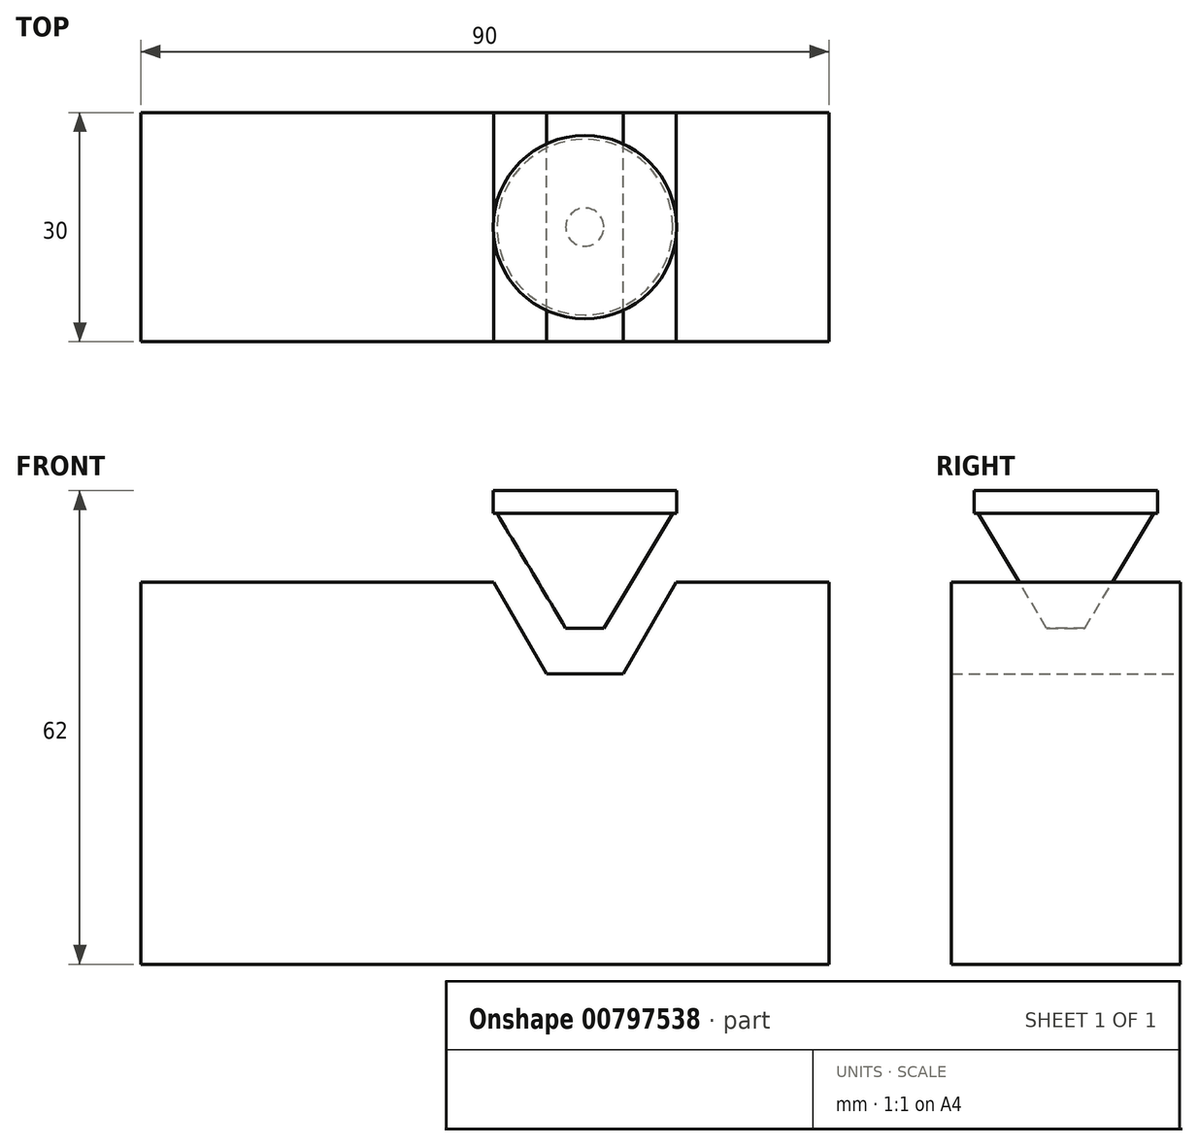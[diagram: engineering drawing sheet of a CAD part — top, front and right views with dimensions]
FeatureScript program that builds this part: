
annotation { "Feature Type Name" : "Feature", "Feature Type Description" : "" }
export const myFeature = defineFeature(function(context is Context, id is Id, definition is map)
    precondition{}
    {
        {
            var Q0;
            Q0=qCreatedBy(makeId("Front.planeOp"),FACE);
            var sketch = newSketch(context, id + "F0", { "sketchPlane" : qUnion([Q0])});
            skLineSegment(sketch, "E0", {"start": v(-90, 50) * mm, "end": v(-43.86, 50) * mm});
            skLineSegment(sketch, "E1", {"start": v(-43.86, 50) * mm, "end": v(-36.93, 38) * mm});
            skLineSegment(sketch, "E2", {"start": v(-36.93, 38) * mm, "end": v(-26.93, 38) * mm});
            skLineSegment(sketch, "E3", {"start": v(-26.93, 38) * mm, "end": v(-20, 50) * mm});
            skLineSegment(sketch, "E4", {"start": v(-20, 50) * mm, "end": v(0, 50) * mm});
            skLineSegment(sketch, "E5", {"start": v(0, 50) * mm, "end": v(0, 0) * mm});
            skLineSegment(sketch, "E6", {"start": v(0, 0) * mm, "end": v(-90, 0) * mm});
            skLineSegment(sketch, "E7", {"start": v(-90, 0) * mm, "end": v(-90, 50) * mm});
            skPoint(sketch, "E8", {"position": v(-31.93, 38) * mm});
            skLineSegment(sketch, "E9.bottom", {"start": v(-31.93, 38) * mm, "end": v(-29.43, 38) * mm});
            skLineSegment(sketch, "E9.top", {"start": v(-31.93, 44) * mm, "end": v(-29.43, 44) * mm});
            skLineSegment(sketch, "E9.left", {"start": v(-31.93, 38) * mm, "end": v(-31.93, 44) * mm});
            skLineSegment(sketch, "E9.right", {"start": v(-29.43, 38) * mm, "end": v(-29.43, 44) * mm});
            skLineSegment(sketch, "E10", {"start": v(-29.43, 44) * mm, "end": v(-20.43, 59) * mm});
            skLineSegment(sketch, "E11", {"start": v(-20.43, 59) * mm, "end": v(-31.93, 59) * mm});
            skLineSegment(sketch, "E12", {"start": v(-31.93, 59) * mm, "end": v(-31.93, 44) * mm});
            skLineSegment(sketch, "E13.bottom", {"start": v(-31.93, 59) * mm, "end": v(-19.93, 59) * mm});
            skLineSegment(sketch, "E13.top", {"start": v(-31.93, 62) * mm, "end": v(-19.93, 62) * mm});
            skLineSegment(sketch, "E13.left", {"start": v(-31.93, 59) * mm, "end": v(-31.93, 62) * mm});
            skLineSegment(sketch, "E13.right", {"start": v(-19.93, 59) * mm, "end": v(-19.93, 62) * mm});
            skSolve(sketch);
        }
        {
            var Q0;
            Q0=makeQuery(id+"F0.imprint","IMPRINT",FACE,{"disambiguationData":[TD([[makeQuery(id+"F0.imprint","IMPRINT",EDGE,{"derivedFrom":sQuery(id+"F0.wireOp",EDGE,"E0")}),-1.0]])]});
            extrude(context, id + "F1", {"entities" : qUnion([Q0]), "endBound" : BoundingType.SYMMETRIC, "depth" : 30 * mm, "offsetDistance" : 25 * mm});
        }
        {
            var Q0;
            Q0=makeQuery(id+"F0.imprint","IMPRINT",FACE,{"disambiguationData":[TD([[makeQuery(id+"F0.imprint","IMPRINT",EDGE,{"derivedFrom":sQuery(id+"F0.wireOp",EDGE,"E9.bottom")}),1.0]])]});
            var Q1;
            Q1=makeQuery(id+"F0.imprint","IMPRINT",FACE,{"disambiguationData":[TD([[makeQuery(id+"F0.imprint","IMPRINT",EDGE,{"derivedFrom":sQuery(id+"F0.wireOp",EDGE,"E9.top")}),1.0]])]});
            var Q2;
            Q2=makeQuery(id+"F0.imprint","IMPRINT",FACE,{"disambiguationData":[TD([[makeQuery(id+"F0.imprint","IMPRINT",EDGE,{"derivedFrom":sQuery(id+"F0.wireOp",EDGE,"E13.top")}),-1.0]])]});
            var Q3;
            Q3=sQuery(id+"F0.wireOp",EDGE,"E9.left");
            revolve(context, id + "F2", {"operationType" : NewBodyOperationType.ADD, "surfaceOperationType" : NewSurfaceOperationType.NEW, "entities" : qUnion([Q0, Q1, Q2]), "axis" : qUnion([Q3]), "revolveType" : RevolveType.FULL});
        }
    });
